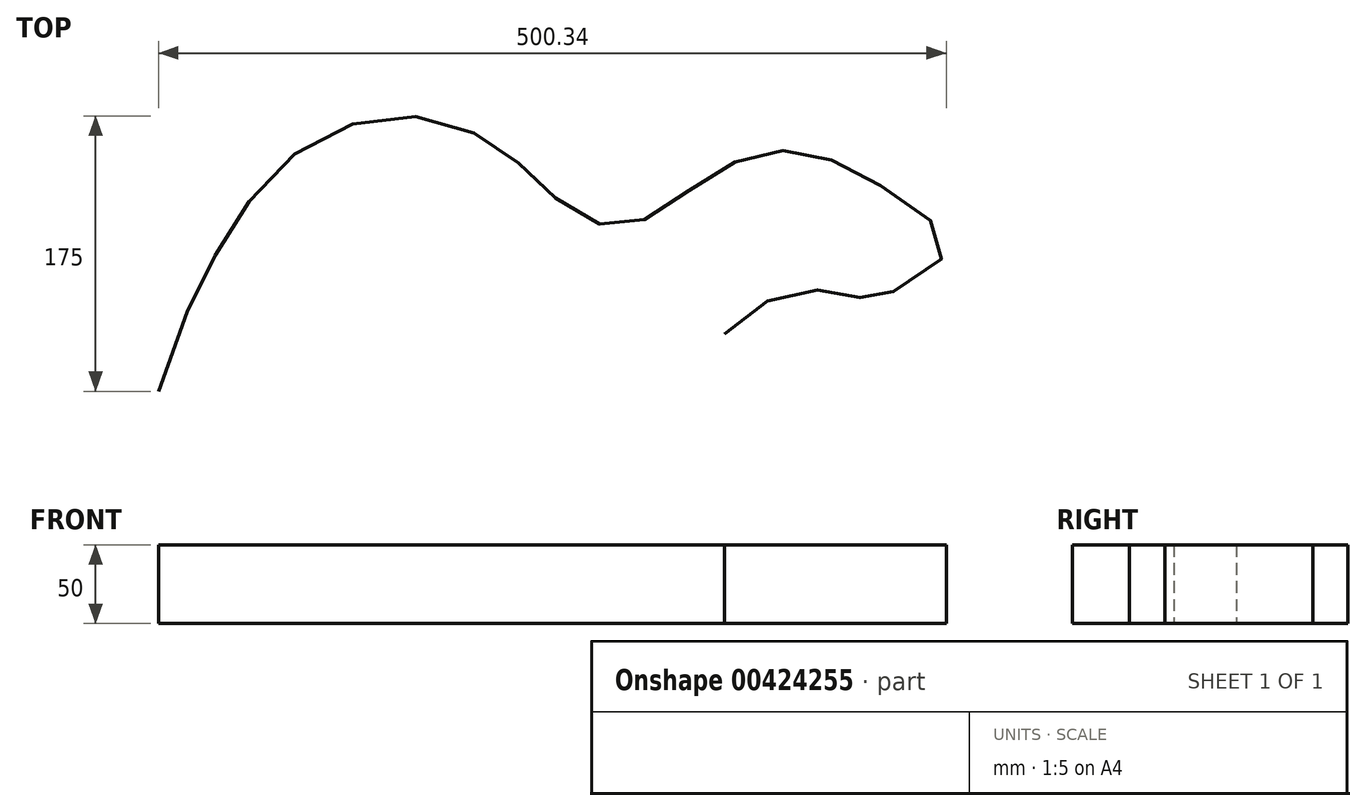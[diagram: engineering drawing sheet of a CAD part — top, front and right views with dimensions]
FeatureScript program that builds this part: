
annotation { "Feature Type Name" : "Feature", "Feature Type Description" : "" }
export const myFeature = defineFeature(function(context is Context, id is Id, definition is map)
    precondition{}
    {
        {
            var Q0;
            Q0=qCreatedBy(makeId("Top.planeOp"),FACE);
            var sketch = newSketch(context, id + "F0", { "sketchPlane" : qUnion([Q0])});
            skLineSegment(sketch, "E0.bottom", {"start": v(-251.3, 175) * mm, "end": v(248.7, 175) * mm, "construction": true});
            skLineSegment(sketch, "E0.top", {"start": v(-251.3, -175) * mm, "end": v(248.7, -175) * mm, "construction": true});
            skLineSegment(sketch, "E0.left", {"start": v(-251.3, 175) * mm, "end": v(-251.3, -175) * mm, "construction": true});
            skLineSegment(sketch, "E0.right", {"start": v(248.7, 175) * mm, "end": v(248.7, -175) * mm, "construction": true});
            skPoint(sketch, "E0.middle", {"position": v(-1.3, 0) * mm});
            skLineSegment(sketch, "E1", {"start": v(-391.4, 0) * mm, "end": v(393.84, 0) * mm, "construction": true});
            skLineSegment(sketch, "E2", {"start": v(0, 195.06) * mm, "end": v(0, -242.32) * mm, "construction": true});
            skLineSegment(sketch, "E3", {"start": v(-251.3, 123.62) * mm, "end": v(261.14, 123.62) * mm, "construction": true});
            skLineSegment(sketch, "E4", {"start": v(-251.3, -86) * mm, "end": v(248.7, -86) * mm, "construction": true});
            skPoint(sketch, "E5", {"position": v(-95.78, 175) * mm});
            skPoint(sketch, "E6", {"position": v(0, 123.62) * mm});
            skPoint(sketch, "E7", {"position": v(-35.73, 155.34) * mm});
            skPoint(sketch, "E8", {"position": v(-251.3, 0) * mm});
            skPoint(sketch, "E9", {"position": v(-213.63, 89.62) * mm});
            skPoint(sketch, "E10", {"position": v(-166.04, 149.68) * mm});
            skPoint(sketch, "E11", {"position": v(40.19, 104.35) * mm});
            skPoint(sketch, "E12", {"position": v(79.85, 123.62) * mm});
            skPoint(sketch, "E13", {"position": v(248.7, 89.62) * mm});
            skPoint(sketch, "E14", {"position": v(168.23, 149.68) * mm});
            skPoint(sketch, "E15", {"position": v(218.08, 123.62) * mm});
            skPoint(sketch, "E16", {"position": v(125.17, 149.68) * mm});
            skPoint(sketch, "E17", {"position": v(206.75, 60.16) * mm});
            skPoint(sketch, "E18", {"position": v(192.02, 60.16) * mm});
            skPoint(sketch, "E19", {"position": v(151.23, 63.56) * mm});
            skPoint(sketch, "E20", {"position": v(108.17, 36.37) * mm});
            skFitSpline(sketch, "E21", {"points": [v(-251.3, 0) * mm, v(-213.63, 89.62) * mm, v(-166.04, 149.68) * mm, v(-95.78, 175) * mm, v(-35.73, 155.34) * mm, v(0, 123.62) * mm, v(40.19, 104.35) * mm, v(79.85, 123.62) * mm, v(125.17, 149.68) * mm, v(168.23, 149.68) * mm, v(218.08, 123.62) * mm, v(248.7, 89.62) * mm, v(206.75, 60.16) * mm, v(192.02, 60.16) * mm, v(151.23, 63.56) * mm, v(108.17, 36.37) * mm], "startDerivative": vector(455.05, 1452.47) * mm, "endDerivative": vector(-615.2, -550.1) * mm});
            skSolve(sketch);
        }
        {
            var Q0;
            Q0=sQuery(id+"F0.wireOp",EDGE,"E21");
            var Q1;
            Q1=sQuery(id+"FKdp7U8cUAFtNLP_0.1.F0.wireOp",EDGE,"E21");
            extrude(context, id + "F1", {"bodyType" : ToolBodyType.SURFACE, "surfaceEntities" : qUnion([Q0, Q1]), "depth" : 50 * mm, "offsetDistance" : 25 * mm});
        }
    });
